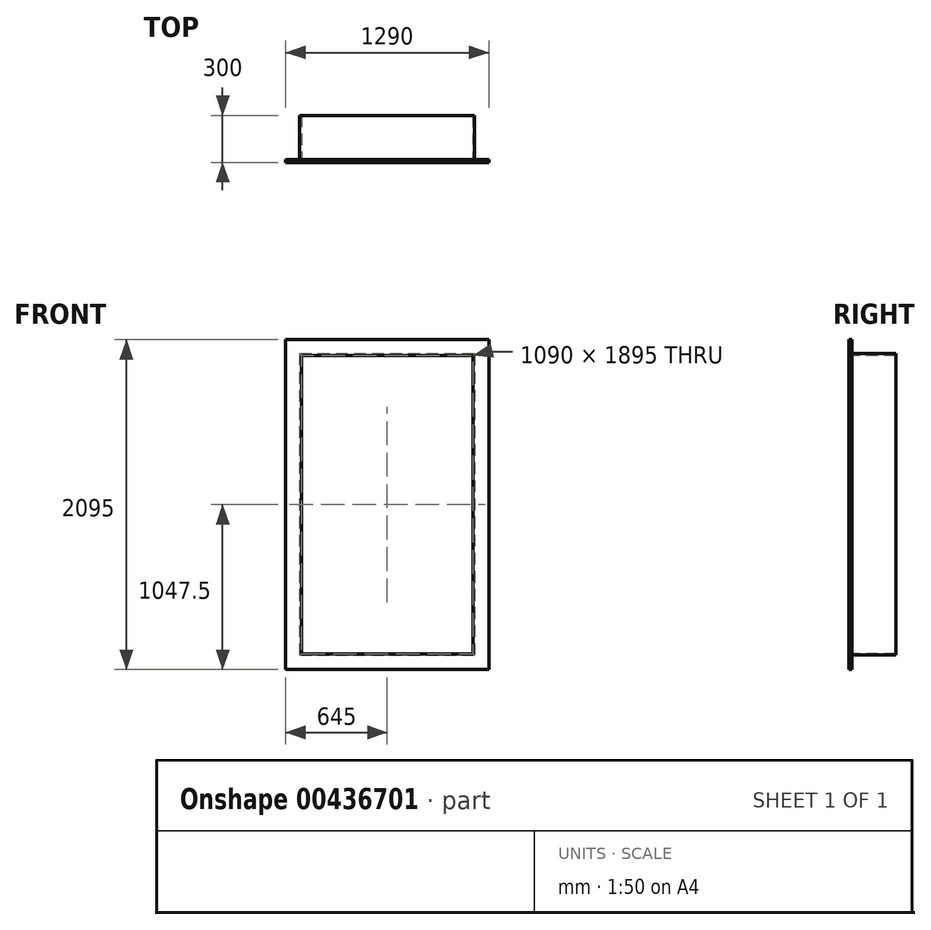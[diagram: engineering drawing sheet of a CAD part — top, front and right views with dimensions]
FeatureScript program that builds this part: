
annotation { "Feature Type Name" : "Feature", "Feature Type Description" : "" }
export const myFeature = defineFeature(function(context is Context, id is Id, definition is map)
    precondition{}
    {
        {
            var Q0;
            Q0=qCreatedBy(makeId("Front.planeOp"),FACE);
            var sketch = newSketch(context, id + "F0", { "sketchPlane" : qUnion([Q0])});
            skLineSegment(sketch, "E0.bottom", {"start": v(-645.35, 1078.55) * mm, "end": v(644.65, 1078.55) * mm});
            skLineSegment(sketch, "E0.top", {"start": v(-645.35, -1016.45) * mm, "end": v(644.65, -1016.45) * mm});
            skLineSegment(sketch, "E0.left", {"start": v(-645.35, 1078.55) * mm, "end": v(-645.35, -1016.45) * mm});
            skLineSegment(sketch, "E0.right", {"start": v(644.65, 1078.55) * mm, "end": v(644.65, -1016.45) * mm});
            skLineSegment(sketch, "E1.bottom", {"start": v(-545.35, 978.55) * mm, "end": v(544.65, 978.55) * mm});
            skLineSegment(sketch, "E1.top", {"start": v(-545.35, -916.45) * mm, "end": v(544.65, -916.45) * mm});
            skLineSegment(sketch, "E1.left", {"start": v(-545.35, 978.55) * mm, "end": v(-545.35, -916.45) * mm});
            skLineSegment(sketch, "E1.right", {"start": v(544.65, 978.55) * mm, "end": v(544.65, -916.45) * mm});
            skSolve(sketch);
        }
        {
            var Q0;
            Q0=makeQuery(id+"F0.imprint","IMPRINT",FACE,{"disambiguationData":[TD([[makeQuery(id+"F0.imprint","IMPRINT",EDGE,{"derivedFrom":sQuery(id+"F0.wireOp",EDGE,"E0.bottom")}),-1.0]])]});
            extrude(context, id + "F1", {"entities" : qUnion([Q0]), "oppositeDirection" : true, "depth" : 20 * mm});
        }
        {
            var Q0;
            Q0=makeQuery(id+"F1.opExtrude","CAP_FACE",FACE,{"disambiguationData":[OSD([sQuery(id+"F0.wireOp",EDGE,"E0.bottom"),sQuery(id+"F0.wireOp",EDGE,"E0.top"),sQuery(id+"F0.wireOp",EDGE,"E0.left"),sQuery(id+"F0.wireOp",EDGE,"E0.right"),sQuery(id+"F0.wireOp",EDGE,"E1.bottom"),sQuery(id+"F0.wireOp",EDGE,"E1.top"),sQuery(id+"F0.wireOp",EDGE,"E1.left"),sQuery(id+"F0.wireOp",EDGE,"E1.right")])],"isStart":true});
            var sketch = newSketch(context, id + "F2", { "sketchPlane" : qUnion([Q0])});
            skLineSegment(sketch, "E2.bottom", {"start": v(-556.98, 990.02) * mm, "end": v(552.93, 990.02) * mm});
            skLineSegment(sketch, "E2.top", {"start": v(-556.98, -924.76) * mm, "end": v(552.93, -924.76) * mm});
            skLineSegment(sketch, "E2.left", {"start": v(-556.98, 990.02) * mm, "end": v(-556.98, -924.76) * mm});
            skLineSegment(sketch, "E2.right", {"start": v(552.93, 990.02) * mm, "end": v(552.93, -924.76) * mm});
            skSolve(sketch);
        }
        {
            var Q0;
            Q0=makeQuery(id+"F2.imprint","IMPRINT",FACE,{"disambiguationData":[TD([[makeQuery(id+"F2.imprint","IMPRINT",EDGE,{"derivedFrom":sQuery(id+"F2.wireOp",EDGE,"E2.bottom")}),-1.0]])]});
            extrude(context, id + "F3", {"entities" : qUnion([Q0]), "operationType" : NewBodyOperationType.ADD, "oppositeDirection" : true, "depth" : 300 * mm});
        }
    });
